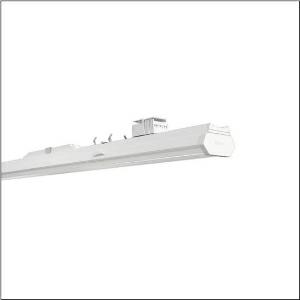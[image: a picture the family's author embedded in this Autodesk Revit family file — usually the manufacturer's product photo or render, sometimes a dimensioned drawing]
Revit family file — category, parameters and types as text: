
# Revit family: licross_21_protected_ho_52td13mn4fxs
name_source: partatom
category: Lighting Fixtures
units: mm (PartAtom-declared; Revit-internal decimal feet)

## family parameters
Cut with Voids When Loaded = No
Host = Face
Light Source = No
Part Type = Normal
Room Calculation Point = No
Round Connector Dimension = Use Diameter
Shared = No

## types (1)
- --- (1 x LED, 15060 lm, 83.2 W, 4000K)
    Apparent Load = 83 VA
    CIE Flux Codes = 89 96 99 100 99
    Color Rendering = 80
    Color Temperature = 4000K
    Default Elevation = 1800 mm
    Description = Licross 21 Protected HO, luminaire insert, of sheet steel, galvanised, coil coated, white, length: 1.500mm, width: 66mm, height: 67mm, LED rated luminous flux: 15.060lm, light colour: 840, SDCM (Standard Deviation of Colour Matching)MacAdam ≤ 3 SDCM (initial), control gear: ON/OFF Multilumen, with plug, 3-pole, with phase selection, mains connection: 220..240V, AC, 50/60Hz, rated input power: 83W, internal wiring halogen-free, primary light control with lens, of plastic, primary optical cover: cover, of PMMA, light emission: direct distribution, primary light characteristic: symmetric, protection rating (complete): IP54, insulation class (complete): insulation class I (protective earthing), certification: CE, ENEC, VDE, UKCA, protection symbol: D if used in an environment with non-conductive dust loads with corresponding accessories, impact resistance: IK06, permissible ambient temperature for indoor applications: -35..+35°C, corresponds to IFS (International Featured Standards) requirements for safety and quality in the food industry, reducing of maximum allowable ambient temperature of 5°C with ceiling mounting, LABS conformity tested according to VDMA 24364:2018-05, The light source and the operating device comply with the requirements of the Ecodesign Regulation (EU) 2019/2020 and are replaceable in accordance with this regulation, packaging unit: 1 piece
    Height = 92 mm
    Lamp = 1 x LED
    Lamp Light Flux = 15060 lm
    Lamp Power = 83.2 W
    Lamp count = 1
    Length = 1500 mm
    Luminous efficacy = 181 lm/W
    Manufacturer = Siteco
    ModVariant = No
    Model = 52TD13MN4FXS
    Mounting Place = Ceiling
    Mounting Type = Pendant
    Number of Poles = 1
    OnlyDefault = Yes
    Power Factor = 1
    Product Name = Licross 21 Protected HO
    Product group = luminaire insert | ceiling pendant
    ProductGroupID = 901
    Protection Class = Protection class I
    Protection Degree = IP 54
    RLX_Detail_Level = 1
    RLX_Emergency_Light_Flux = 0 lm
    RLX_Emergency_Type = 0
    RLX_Emergency_Type_DB = No
    RlxData = <blob elided: 22161 chars, md5=9f5ca698>
    Socket = socket
    Standby Power = 0 W
    System Light Flux = 15060 lm
    System Power = 83 W
    Type Comments = factory setting: luminous flux: 100 % | (A | C | E) | 195 mA
    Type Image = l_1256148.jpg
    URL = http://relux.com
    VarID = @adj_108991
    Voltage = 0 V
    Weight = 0.00 kg
    Width = 88 mm

## geometry (parser evidence)
native form markers: Blend x4, Sweep x11
no freeform markers — native parametric forms only
